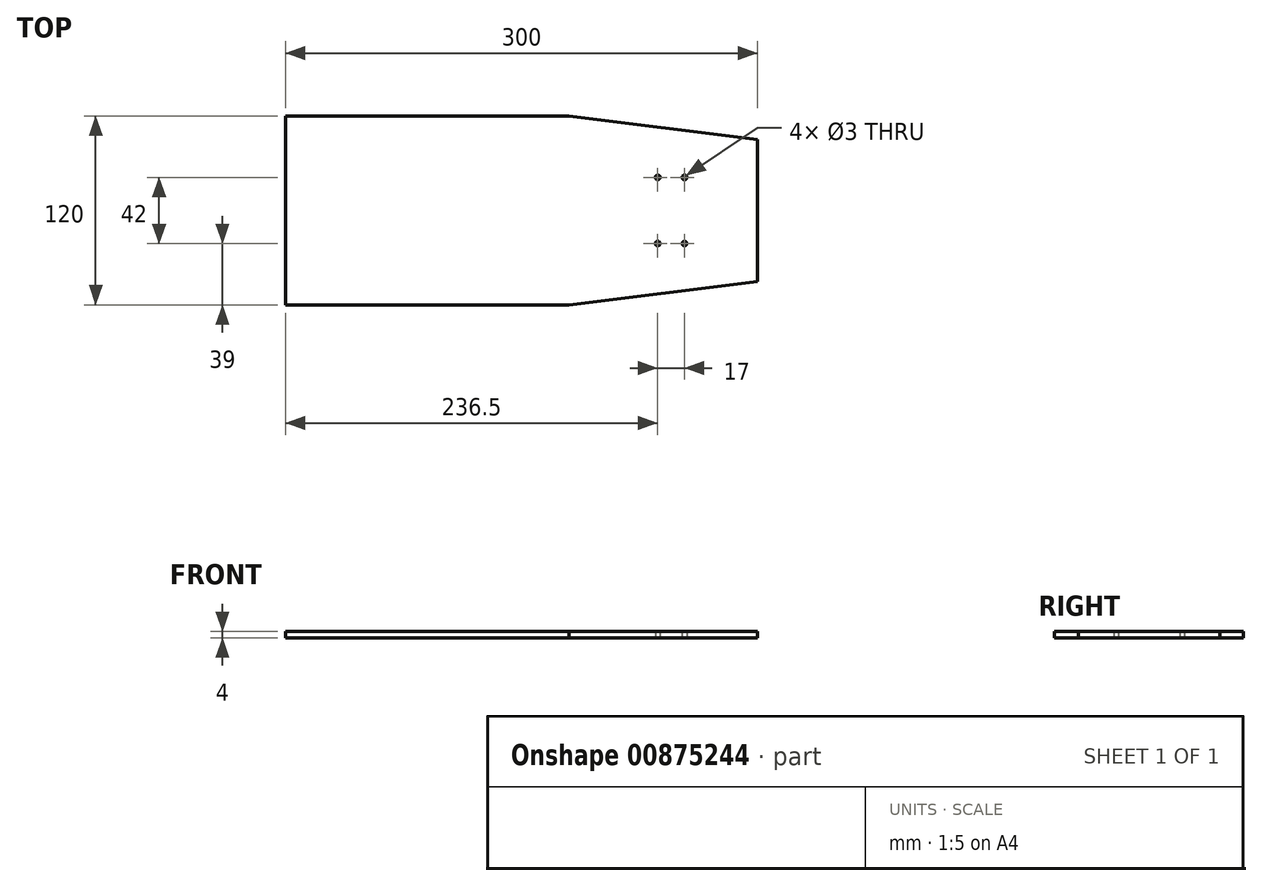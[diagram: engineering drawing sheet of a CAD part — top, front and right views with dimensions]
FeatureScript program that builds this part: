
annotation { "Feature Type Name" : "Feature", "Feature Type Description" : "" }
export const myFeature = defineFeature(function(context is Context, id is Id, definition is map)
    precondition{}
    {
        {
            var Q0;
            Q0=qCreatedBy(makeId("Top.planeOp"),FACE);
            var sketch = newSketch(context, id + "F0", { "sketchPlane" : qUnion([Q0])});
            skLineSegment(sketch, "E0", {"start": v(0, 60) * mm, "end": v(0, -60) * mm});
            skLineSegment(sketch, "E1", {"start": v(0, -60) * mm, "end": v(180, -60) * mm});
            skLineSegment(sketch, "E2", {"start": v(180, -60) * mm, "end": v(300, -45) * mm});
            skLineSegment(sketch, "E3", {"start": v(300, -45) * mm, "end": v(300, 45) * mm});
            skLineSegment(sketch, "E4", {"start": v(300, 45) * mm, "end": v(180, 60) * mm});
            skLineSegment(sketch, "E5", {"start": v(180, 60) * mm, "end": v(0, 60) * mm});
            skLineSegment(sketch, "E6", {"start": v(0, 0) * mm, "end": v(300, 0) * mm, "construction": true});
            skLineSegment(sketch, "E7", {"start": v(180, 60) * mm, "end": v(180, -60) * mm, "construction": true});
            skCircle(sketch, "E8", {"center": v(253.5, -21) * mm, "radius": 1.5 * mm});
            skCircle(sketch, "E9", {"center": v(236.5, -21) * mm, "radius": 1.5 * mm});
            skLineSegment(sketch, "E10", {"start": v(253.5, -21) * mm, "end": v(236.5, -21) * mm, "construction": true});
            skCircle(sketch, "E11", {"center": v(253.5, 21) * mm, "radius": 1.5 * mm});
            skCircle(sketch, "E12", {"center": v(236.5, 21) * mm, "radius": 1.5 * mm});
            skLineSegment(sketch, "E13", {"start": v(253.5, 21) * mm, "end": v(236.5, 21) * mm, "construction": true});
            skLineSegment(sketch, "E14", {"start": v(245, -21) * mm, "end": v(245, 21) * mm, "construction": true});
            skLineSegment(sketch, "E15", {"start": v(300, 0) * mm, "end": v(245, 0) * mm, "construction": true});
            skSolve(sketch);
        }
        {
            var Q0;
            Q0 = qSketchRegion(id + "F0", true);
            extrude(context, id + "F1", {"entities" : qUnion([Q0]), "depth" : 4 * mm, "offsetDistance" : 25 * mm});
        }
    });
